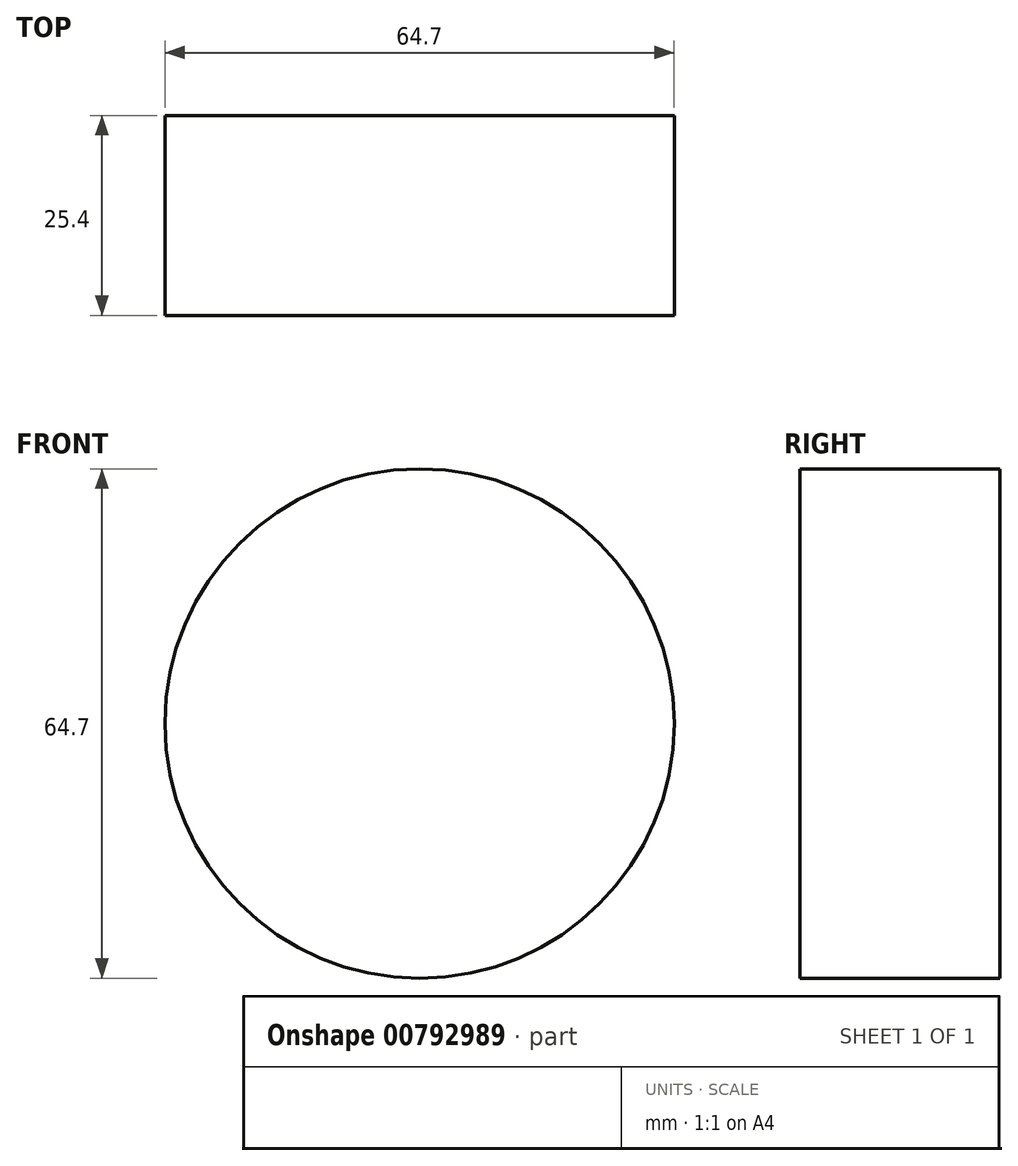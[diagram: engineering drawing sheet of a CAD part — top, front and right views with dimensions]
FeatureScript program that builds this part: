
annotation { "Feature Type Name" : "Feature", "Feature Type Description" : "" }
export const myFeature = defineFeature(function(context is Context, id is Id, definition is map)
    precondition{}
    {
        {
            var Q0;
            Q0=qCreatedBy(makeId("Front.planeOp"),FACE);
            var sketch = newSketch(context, id + "F0", { "sketchPlane" : qUnion([Q0])});
            skCircle(sketch, "E0", {"center": v(0, 0) * mm, "radius": 32.35 * mm});
            skSolve(sketch);
        }
        {
            var Q0;
            Q0=makeQuery(id+"F0.imprint","IMPRINT",FACE,{"disambiguationData":[TD([[makeQuery(id+"F0.imprint","IMPRINT",EDGE,{"derivedFrom":sQuery(id+"F0.wireOp",EDGE,"E0")}),1.0]])]});
            extrude(context, id + "F1", {"entities" : qUnion([Q0]), "depth" : 25.4 * mm, "offsetDistance" : 25.4 * mm});
        }
    });
